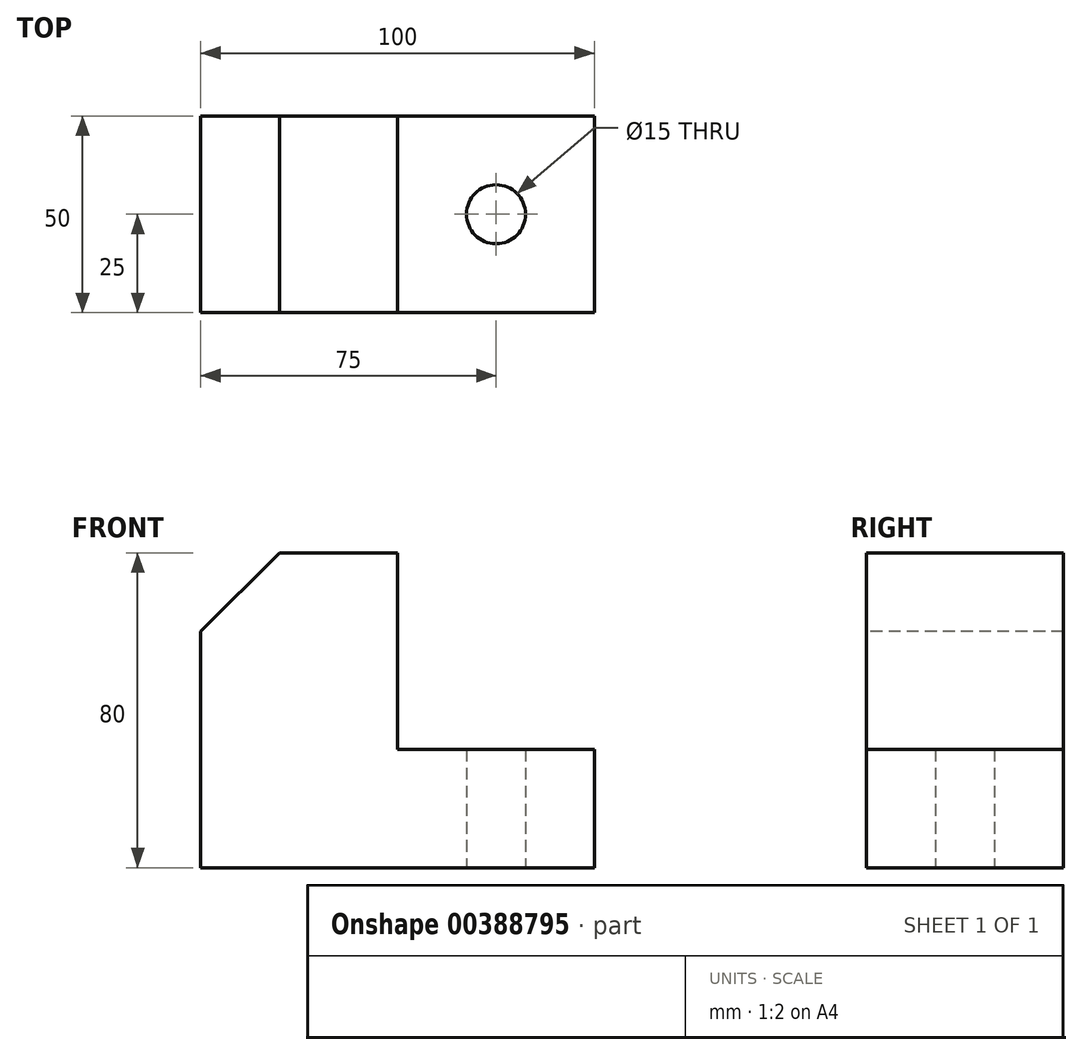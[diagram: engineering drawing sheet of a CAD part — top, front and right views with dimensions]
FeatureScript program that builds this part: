
annotation { "Feature Type Name" : "Feature", "Feature Type Description" : "" }
export const myFeature = defineFeature(function(context is Context, id is Id, definition is map)
    precondition{}
    {
        {
            var Q0;
            Q0=qCreatedBy(makeId("Top.planeOp"),FACE);
            var sketch = newSketch(context, id + "F0", { "sketchPlane" : qUnion([Q0])});
            skLineSegment(sketch, "E0.bottom", {"start": v(0, 0) * mm, "end": v(100, 0) * mm});
            skLineSegment(sketch, "E0.top", {"start": v(0, 50) * mm, "end": v(100, 50) * mm});
            skLineSegment(sketch, "E0.left", {"start": v(0, 0) * mm, "end": v(0, 50) * mm});
            skLineSegment(sketch, "E0.right", {"start": v(100, 0) * mm, "end": v(100, 50) * mm});
            skSolve(sketch);
        }
        {
            var Q0;
            Q0 = qSketchRegion(id + "F0", true);
            extrude(context, id + "F1", {"entities" : qUnion([Q0]), "depth" : 30 * mm});
        }
        {
            var Q0;
            Q0=makeQuery(id+"F1.opExtrude","CAP_FACE",FACE,{"disambiguationData":[OSD([sQuery(id+"F0.wireOp",EDGE,"E0.bottom"),sQuery(id+"F0.wireOp",EDGE,"E0.top"),sQuery(id+"F0.wireOp",EDGE,"E0.left"),sQuery(id+"F0.wireOp",EDGE,"E0.right")])],"isStart":false});
            var sketch = newSketch(context, id + "F2", { "sketchPlane" : qUnion([Q0])});
            skLineSegment(sketch, "E1.bottom", {"start": v(0, 0) * mm, "end": v(50, 0) * mm});
            skLineSegment(sketch, "E1.top", {"start": v(0, 50) * mm, "end": v(50, 50) * mm});
            skLineSegment(sketch, "E1.left", {"start": v(0, 0) * mm, "end": v(0, 50) * mm});
            skLineSegment(sketch, "E1.right", {"start": v(50, 0) * mm, "end": v(50, 50) * mm});
            skSolve(sketch);
        }
        {
            var Q0;
            Q0 = qSketchRegion(id + "F2", true);
            extrude(context, id + "F3", {"entities" : qUnion([Q0]), "operationType" : NewBodyOperationType.ADD, "depth" : 50 * mm});
        }
        {
            var Q0;
            Q0=makeQuery(id+"F3.boolean.opBoolean","MERGE",FACE,{"derivedFrom":[makeQuery(id+"F1.opExtrude","SWEPT_FACE",FACE,{"disambiguationData":[OSD([sQuery(id+"F0.wireOp",EDGE,"E0.bottom")])]}),makeQuery(id+"F3.opExtrude","SWEPT_FACE",FACE,{"disambiguationData":[OSD([sQuery(id+"F2.wireOp",EDGE,"E1.bottom")])]})]});
            var sketch = newSketch(context, id + "F4", { "sketchPlane" : qUnion([Q0])});
            skLineSegment(sketch, "E2", {"start": v(0, 80) * mm, "end": v(20, 80) * mm});
            skLineSegment(sketch, "E3", {"start": v(0, 80) * mm, "end": v(0, 60) * mm});
            skLineSegment(sketch, "E4", {"start": v(0, 60) * mm, "end": v(20, 80) * mm});
            skSolve(sketch);
        }
        {
            var Q0;
            Q0 = qSketchRegion(id + "F4", true);
            extrude(context, id + "F5", {"entities" : qUnion([Q0]), "operationType" : NewBodyOperationType.REMOVE, "endBound" : BoundingType.UP_TO_NEXT, "oppositeDirection" : true, "depth" : 25 * mm});
        }
        {
            var Q0;
            Q0=makeQuery(id+"F1.opExtrude","CAP_FACE",FACE,{"disambiguationData":[OSD([sQuery(id+"F0.wireOp",EDGE,"E0.bottom"),sQuery(id+"F0.wireOp",EDGE,"E0.top"),sQuery(id+"F0.wireOp",EDGE,"E0.left"),sQuery(id+"F0.wireOp",EDGE,"E0.right")])],"isStart":true});
            var sketch = newSketch(context, id + "F6", { "sketchPlane" : qUnion([Q0])});
            skLineSegment(sketch, "E5", {"start": v(0, -50) * mm, "end": v(55.3, -50) * mm});
            skLineSegment(sketch, "E6.bottom", {"start": v(0, -50) * mm, "end": v(75, -50) * mm});
            skLineSegment(sketch, "E6.top", {"start": v(0, -25) * mm, "end": v(75, -25) * mm});
            skLineSegment(sketch, "E6.left", {"start": v(0, -50) * mm, "end": v(0, -25) * mm});
            skLineSegment(sketch, "E6.right", {"start": v(75, -50) * mm, "end": v(75, -25) * mm});
            skCircle(sketch, "E7", {"center": v(75, -25) * mm, "radius": 7.5 * mm});
            skSolve(sketch);
        }
        {
            var Q0;
            {var subQ0=sQuery(id+"F6.wireOp",EDGE,"E6.right");var subQ1=sQuery(id+"F6.wireOp",EDGE,"E6.top");var subQ2=makeQuery(id+"F6.imprint","INTERSECT",VERTEX,{"derivedFrom":[subQ1,subQ0]});Q0=makeQuery(id+"F6.imprint","IMPRINT",FACE,{"disambiguationData":[TD([[makeQuery(id+"F6.imprint","IMPRINT",EDGE,{"disambiguationData":[TD([[subQ2,1.0]])],"derivedFrom":subQ1}),-1.0]])]});}
            var Q1;
            {var subQ0=sQuery(id+"F6.wireOp",EDGE,"E6.right");var subQ1=sQuery(id+"F6.wireOp",EDGE,"E6.top");var subQ2=makeQuery(id+"F6.imprint","INTERSECT",VERTEX,{"derivedFrom":[subQ1,subQ0]});Q1=makeQuery(id+"F6.imprint","IMPRINT",FACE,{"disambiguationData":[TD([[makeQuery(id+"F6.imprint","IMPRINT",EDGE,{"disambiguationData":[TD([[subQ2,1.0]])],"derivedFrom":subQ1}),1.0]])]});}
            extrude(context, id + "F7", {"entities" : qUnion([Q0, Q1]), "operationType" : NewBodyOperationType.REMOVE, "endBound" : BoundingType.UP_TO_NEXT, "oppositeDirection" : true, "depth" : 25 * mm});
        }
    });
